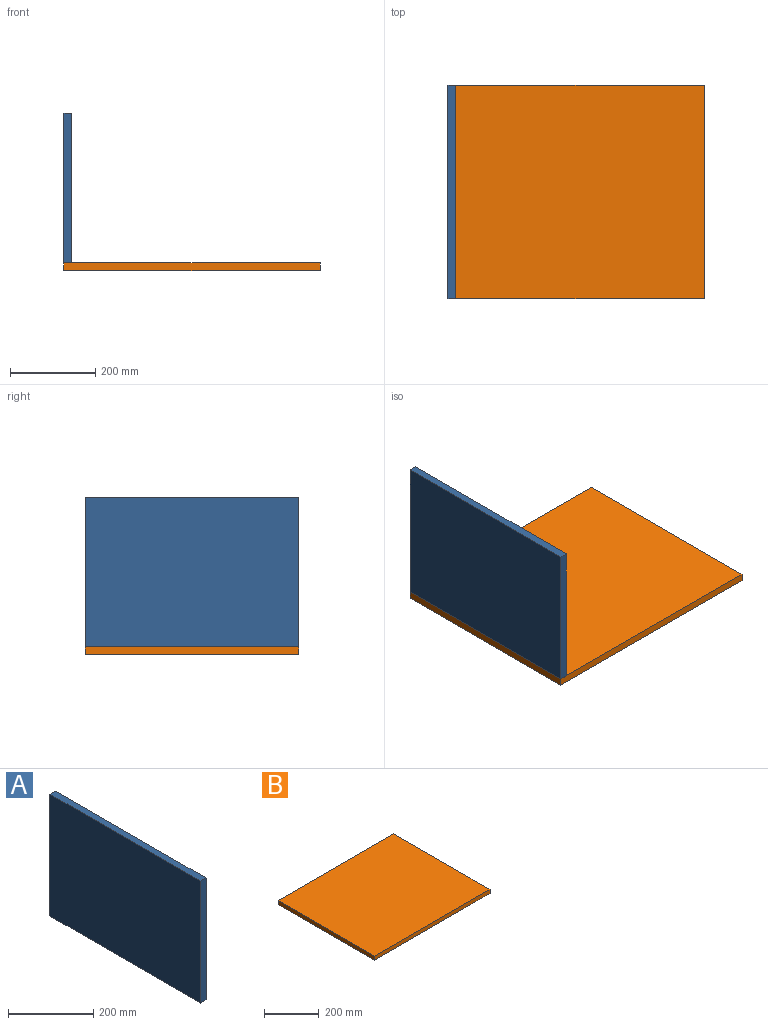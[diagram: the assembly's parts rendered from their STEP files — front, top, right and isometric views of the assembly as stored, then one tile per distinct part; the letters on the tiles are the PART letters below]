
ASSEMBLY  parts=2 mates=1
PART A: 6 faces, bbox 18x500x350 mm
  f0: plane 350x18mm, normal (0,1,0), area 6300mm2, adj f1,f3,f4,f5
  f1: plane 500x18mm, normal (0,0,1), area 9000mm2, adj f0,f2,f4,f5
  f2: plane 350x18mm, normal (0,-1,0), area 6300mm2, adj f1,f3,f4,f5
  f3: plane 500x18mm, normal (0,0,-1), area 9000mm2, adj f0,f2,f4,f5
  f4: plane 500x350mm, normal (1,0,0), area 175000mm2, adj f0,f1,f2,f3
  f5: plane 500x350mm, normal (-1,0,0), area 175000mm2, adj f0,f1,f2,f3
PART B: 6 faces, bbox 600x500x18 mm
  f0: plane 500x18mm, normal (1,0,0), area 9000mm2, adj f1,f3,f4,f5
  f1: plane 600x18mm, normal (0,1,0), area 10800mm2, adj f0,f2,f4,f5
  f2: plane 500x18mm, normal (-1,0,0), area 9000mm2, adj f1,f3,f4,f5
  f3: plane 600x18mm, normal (0,-1,0), area 10800mm2, adj f0,f2,f4,f5
  f4: plane 600x500mm, normal (0,0,1), area 300000mm2, adj f0,f1,f2,f3
  f5: plane 600x500mm, normal (0,0,-1), area 300000mm2, adj f0,f1,f2,f3
PLACE A t=(-300,0,193)mm
PLACE B at identity fixed
MATE fastened A.f3 <-> B.f4  axis (0,0,-1) through (-300,0,18)mm
